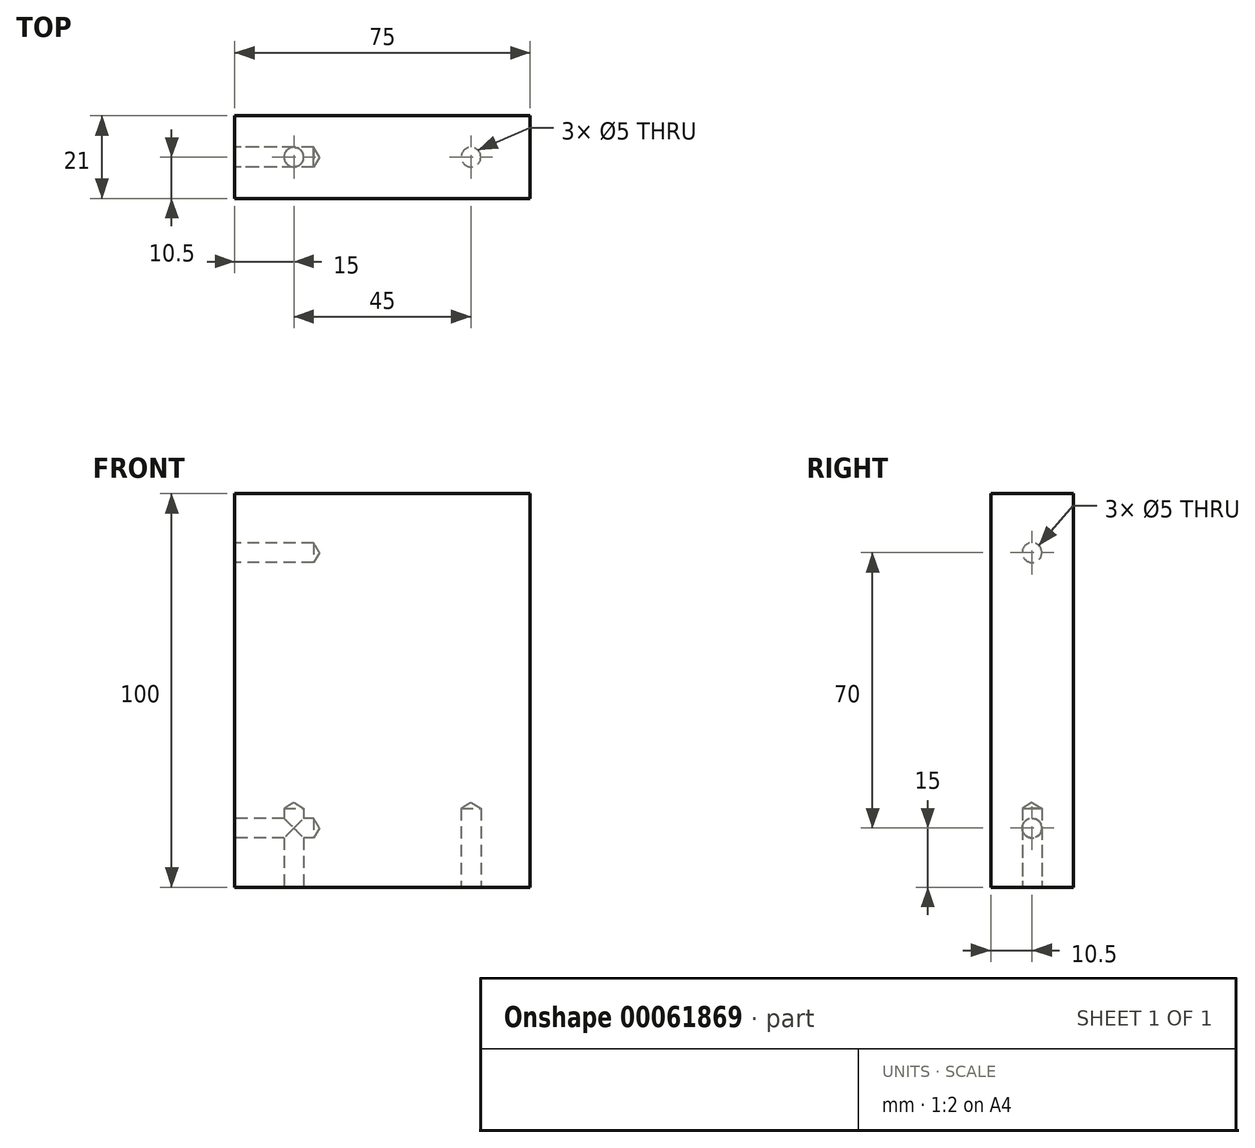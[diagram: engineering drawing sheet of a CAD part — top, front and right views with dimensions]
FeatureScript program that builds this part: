
annotation { "Feature Type Name" : "Feature", "Feature Type Description" : "" }
export const myFeature = defineFeature(function(context is Context, id is Id, definition is map)
    precondition{}
    {
        {
            var Q0;
            Q0=qCreatedBy(makeId("Front.planeOp"),FACE);
            var sketch = newSketch(context, id + "F0", { "sketchPlane" : qUnion([Q0])});
            skLineSegment(sketch, "E0.bottom", {"start": v(0, 0) * mm, "end": v(75, 0) * mm});
            skLineSegment(sketch, "E0.top", {"start": v(0, 100) * mm, "end": v(75, 100) * mm});
            skLineSegment(sketch, "E0.left", {"start": v(0, 0) * mm, "end": v(0, 100) * mm});
            skLineSegment(sketch, "E0.right", {"start": v(75, 0) * mm, "end": v(75, 100) * mm});
            skSolve(sketch);
        }
        {
            var Q0;
            Q0 = qSketchRegion(id + "F0", true);
            extrude(context, id + "F1", {"entities" : qUnion([Q0]), "depth" : 21 * mm});
        }
        {
            var Q0;
            Q0=makeQuery(id+"F1.opExtrude","SWEPT_FACE",FACE,{"disambiguationData":[OSD([sQuery(id+"F0.wireOp",EDGE,"E0.left")])]});
            var sketch = newSketch(context, id + "F2", { "sketchPlane" : qUnion([Q0])});
            skLineSegment(sketch, "E1", {"start": v(10.5, 100) * mm, "end": v(10.5, 0) * mm, "construction": true});
            skPoint(sketch, "E2", {"position": v(10.5, 15) * mm});
            skPoint(sketch, "E3", {"position": v(10.5, 85) * mm});
            skSolve(sketch);
        }
        {
            var Q0;
            Q0=makeQuery(id+"F1.opExtrude","SWEPT_FACE",FACE,{"disambiguationData":[OSD([sQuery(id+"F0.wireOp",EDGE,"E0.bottom")])]});
            var sketch = newSketch(context, id + "F3", { "sketchPlane" : qUnion([Q0])});
            skLineSegment(sketch, "E4", {"start": v(0, 10.5) * mm, "end": v(75, 10.5) * mm, "construction": true});
            skPoint(sketch, "E5", {"position": v(15, 10.5) * mm});
            skPoint(sketch, "E6", {"position": v(60, 10.5) * mm});
            skSolve(sketch);
        }
        {
            var Q0;
            Q0=sQuery(id+"F2.wireOp",VERTEX,"E2");
            var Q1;
            Q1=sQuery(id+"F2.wireOp",VERTEX,"E3");
            var Q2;
            Q2=sQuery(id+"F3.wireOp",VERTEX,"E5");
            var Q3;
            Q3=sQuery(id+"F3.wireOp",VERTEX,"E6");
            var Q4;
            Q4=makeQuery(id+"F1.opExtrude","SWEPT_BODY",BODY,{"disambiguationData":[OSD([sQuery(id+"F0.wireOp",EDGE,"E0.bottom"),sQuery(id+"F0.wireOp",EDGE,"E0.top"),sQuery(id+"F0.wireOp",EDGE,"E0.left"),sQuery(id+"F0.wireOp",EDGE,"E0.right")])]});
            hole(context, id + "F4", {"style" : HoleStyle.SIMPLE, "holeDiameter" : 5 * mm, "endStyle" : HoleEndStyle.BLIND, "holeDepth" : 20 * mm, "locations" : qUnion([Q0, Q1, Q2, Q3]), "scope" : qUnion([Q4])});
        }
    });
